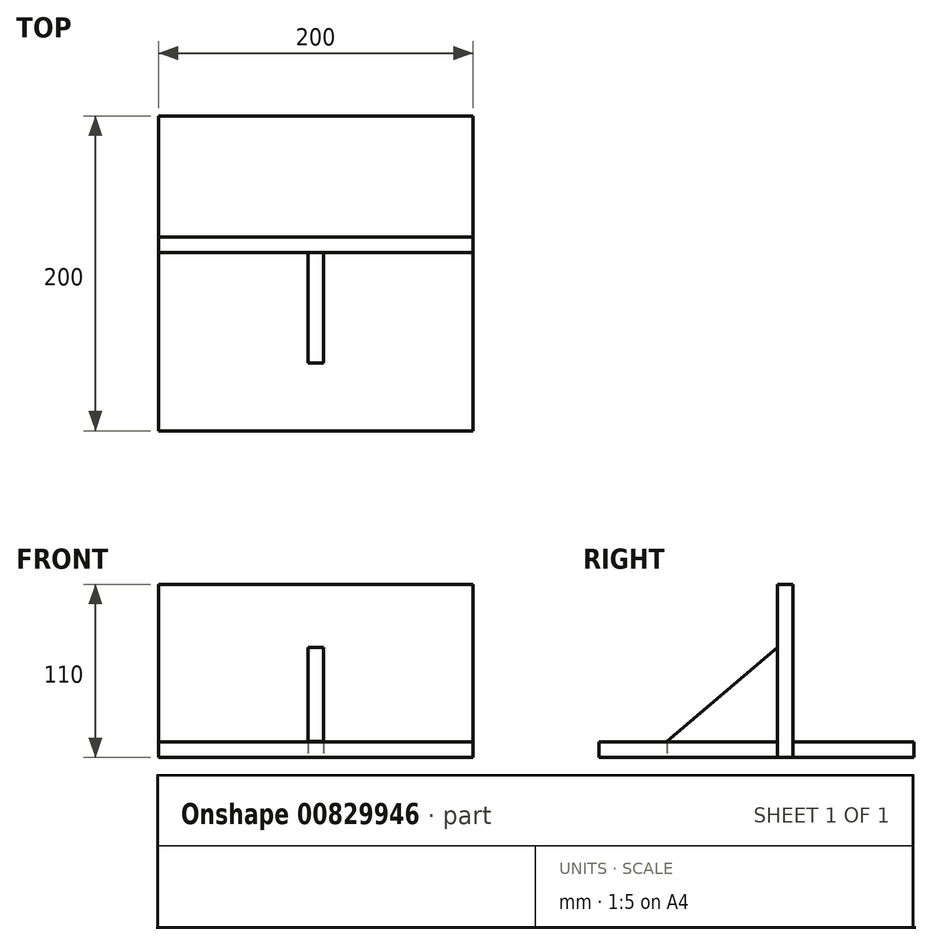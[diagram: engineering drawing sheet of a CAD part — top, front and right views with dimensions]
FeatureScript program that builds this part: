
annotation { "Feature Type Name" : "Feature", "Feature Type Description" : "" }
export const myFeature = defineFeature(function(context is Context, id is Id, definition is map)
    precondition{}
    {
        {
            var Q0;
            Q0=qCreatedBy(makeId("Top.planeOp"),FACE);
            var sketch = newSketch(context, id + "F0", { "sketchPlane" : qUnion([Q0])});
            skLineSegment(sketch, "E0.bottom", {"start": v(-100, 100) * mm, "end": v(100, 100) * mm});
            skLineSegment(sketch, "E0.top", {"start": v(-100, -100) * mm, "end": v(100, -100) * mm});
            skLineSegment(sketch, "E0.left", {"start": v(-100, 100) * mm, "end": v(-100, -100) * mm});
            skLineSegment(sketch, "E0.right", {"start": v(100, 100) * mm, "end": v(100, -100) * mm});
            skPoint(sketch, "E0.middle", {"position": v(0, 0) * mm});
            skLineSegment(sketch, "E1", {"start": v(-100, 13.2) * mm, "end": v(100, 13.2) * mm});
            skLineSegment(sketch, "E2", {"start": v(-100, 23.2) * mm, "end": v(100, 23.2) * mm});
            skLineSegment(sketch, "E3.bottom", {"start": v(-20.44, 13.2) * mm, "end": v(25.44, 13.2) * mm});
            skLineSegment(sketch, "E3.top", {"start": v(-20.44, 13.2) * mm, "end": v(25.44, 13.2) * mm});
            skLineSegment(sketch, "E3.left", {"start": v(-20.44, 13.2) * mm, "end": v(-20.44, 13.2) * mm});
            skLineSegment(sketch, "E3.right", {"start": v(25.44, 13.2) * mm, "end": v(25.44, 13.2) * mm});
            skLineSegment(sketch, "E4", {"start": v(-5, 13.2) * mm, "end": v(0, 13.2) * mm});
            skLineSegment(sketch, "E5", {"start": v(0, 13.2) * mm, "end": v(0, -56.8) * mm});
            skLineSegment(sketch, "E6", {"start": v(0, -56.8) * mm, "end": v(-5, -56.8) * mm});
            skLineSegment(sketch, "E7", {"start": v(-5, -56.8) * mm, "end": v(-5, 13.2) * mm});
            skLineSegment(sketch, "E8", {"start": v(0, 13.2) * mm, "end": v(5, 13.2) * mm});
            skLineSegment(sketch, "E9", {"start": v(5, 13.2) * mm, "end": v(5, -56.8) * mm});
            skLineSegment(sketch, "E10", {"start": v(5, -56.8) * mm, "end": v(0, -56.8) * mm});
            skSolve(sketch);
        }
        {
            var Q0;
            {var subQ0=sQuery(id+"F0.wireOp",EDGE,"E0.bottom");Q0=makeQuery(id+"F0.imprint","IMPRINT",FACE,{"disambiguationData":[TD([[makeQuery(id+"F0.imprint","IMPRINT",EDGE,{"derivedFrom":subQ0}),-1.0]])]});}
            var Q1;
            {var subQ7=sQuery(id+"F0.wireOp",EDGE,"E0.top");Q1=makeQuery(id+"F0.imprint","IMPRINT",FACE,{"disambiguationData":[TD([[makeQuery(id+"F0.imprint","IMPRINT",EDGE,{"derivedFrom":subQ7}),1.0]])]});}
            extrude(context, id + "F1", {"entities" : qUnion([Q0, Q1]), "depth" : 10 * mm, "offsetDistance" : 25 * mm});
        }
        {
            var Q0;
            {var subQ6=sQuery(id+"F0.wireOp",EDGE,"E2");Q0=makeQuery(id+"F0.imprint","IMPRINT",FACE,{"disambiguationData":[TD([[makeQuery(id+"F0.imprint","IMPRINT",EDGE,{"derivedFrom":subQ6}),-1.0]])]});}
            extrude(context, id + "F2", {"entities" : qUnion([Q0]), "depth" : 110 * mm, "offsetDistance" : 25 * mm});
        }
        {
            var Q0;
            {var subQ2=sQuery(id+"F0.wireOp",EDGE,"E5");Q0=makeQuery(id+"F0.imprint","IMPRINT",FACE,{"disambiguationData":[TD([[makeQuery(id+"F0.imprint","IMPRINT",EDGE,{"derivedFrom":subQ2}),1.0]])]});}
            var Q1;
            {var subQ0=sQuery(id+"F0.wireOp",EDGE,"E5");Q1=makeQuery(id+"F0.imprint","IMPRINT",FACE,{"disambiguationData":[TD([[makeQuery(id+"F0.imprint","IMPRINT",EDGE,{"derivedFrom":subQ0}),-1.0]])]});}
            extrude(context, id + "F3", {"entities" : qUnion([Q0, Q1]), "depth" : 70 * mm, "offsetDistance" : 25 * mm});
        }
        {
            var Q0;
            Q0=makeQuery(id+"F3.opExtrude","SWEPT_FACE",FACE,{"disambiguationData":[OSD([sQuery(id+"F0.wireOp",EDGE,"E7")])]});
            var sketch = newSketch(context, id + "F4", { "sketchPlane" : qUnion([Q0])});
            skLineSegment(sketch, "E11", {"start": v(-13.2, 70) * mm, "end": v(56.8, 10.28) * mm});
            skLineSegment(sketch, "E12", {"start": v(56.8, 10.28) * mm, "end": v(-13.2, 10.28) * mm});
            skLineSegment(sketch, "E13", {"start": v(-13.2, 10.28) * mm, "end": v(-13.2, 70) * mm});
            skLineSegment(sketch, "E14", {"start": v(-13.2, 70) * mm, "end": v(56.8, 70) * mm});
            skLineSegment(sketch, "E15", {"start": v(56.8, 70) * mm, "end": v(56.8, 10.28) * mm});
            skSolve(sketch);
        }
        {
            var Q0;
            Q0=makeQuery(id+"F4.imprint","IMPRINT",FACE,{"disambiguationData":[TD([[makeQuery(id+"F4.imprint","IMPRINT",EDGE,{"derivedFrom":sQuery(id+"F4.wireOp",EDGE,"E11")}),1.0]])]});
            extrude(context, id + "F5", {"entities" : qUnion([Q0]), "operationType" : NewBodyOperationType.REMOVE, "oppositeDirection" : true, "depth" : 100 * mm, "offsetDistance" : 25 * mm});
        }
    });
